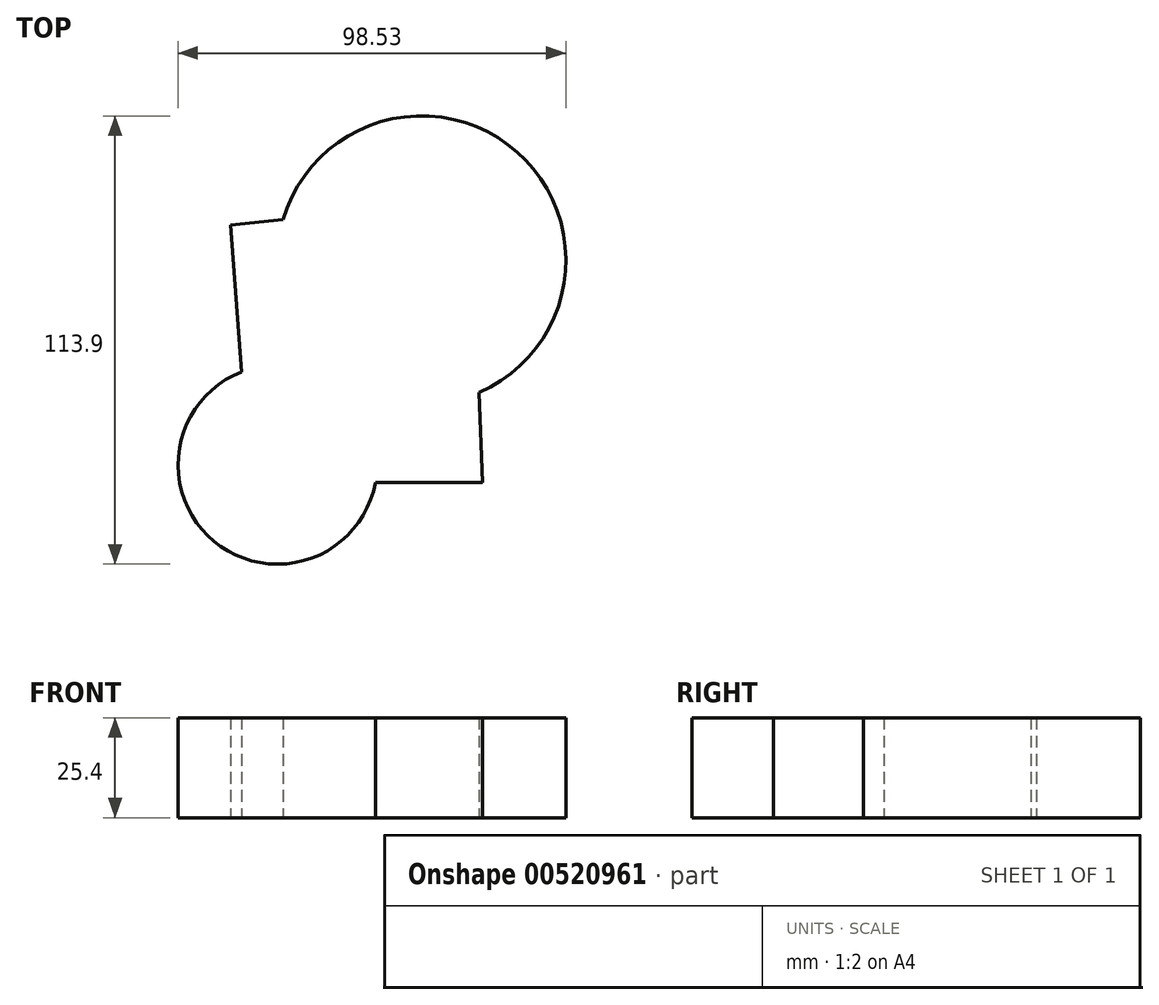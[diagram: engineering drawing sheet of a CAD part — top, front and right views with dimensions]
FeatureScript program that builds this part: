
annotation { "Feature Type Name" : "Feature", "Feature Type Description" : "" }
export const myFeature = defineFeature(function(context is Context, id is Id, definition is map)
    precondition{}
    {
        {
            var Q0;
            Q0=qCreatedBy(makeId("Top.planeOp"),FACE);
            var sketch = newSketch(context, id + "F0", { "sketchPlane" : qUnion([Q0])});
            skLineSegment(sketch, "E0", {"start": v(-48.47, 42.93) * mm, "end": v(-43.8, -19.86) * mm});
            skLineSegment(sketch, "E1", {"start": v(-43.8, -22.48) * mm, "end": v(15.48, -22.48) * mm});
            skLineSegment(sketch, "E2", {"start": v(15.48, -22.48) * mm, "end": v(12.85, 49.35) * mm});
            skLineSegment(sketch, "E3", {"start": v(12.85, 49.35) * mm, "end": v(-48.47, 42.93) * mm});
            skLineSegment(sketch, "E4", {"start": v(-43.8, -22.48) * mm, "end": v(-44.29, -13.34) * mm});
            skCircle(sketch, "E5", {"center": v(0, 34.04) * mm, "radius": 36.66 * mm});
            skCircle(sketch, "E6", {"center": v(-36.6, -17.94) * mm, "radius": 25.26 * mm});
            skSolve(sketch);
        }
        {
            var Q0;
            {var subQ0=sQuery(id+"F0.wireOp",EDGE,"E3");var subQ1=sQuery(id+"F0.wireOp",EDGE,"E2");var subQ2=makeQuery(id+"F0.imprint","INTERSECT",VERTEX,{"derivedFrom":[subQ1,subQ0]});Q0=makeQuery(id+"F0.imprint","IMPRINT",FACE,{"disambiguationData":[TD([[makeQuery(id+"F0.imprint","IMPRINT",EDGE,{"disambiguationData":[TD([[subQ2,1.0]])],"derivedFrom":subQ1}),1.0]])]});}
            var Q1;
            {var subQ0=sQuery(id+"F0.wireOp",EDGE,"E3");var subQ1=sQuery(id+"F0.wireOp",EDGE,"E2");var subQ2=makeQuery(id+"F0.imprint","INTERSECT",VERTEX,{"derivedFrom":[subQ1,subQ0]});Q1=makeQuery(id+"F0.imprint","IMPRINT",FACE,{"disambiguationData":[TD([[makeQuery(id+"F0.imprint","IMPRINT",EDGE,{"disambiguationData":[TD([[subQ2,1.0]])],"derivedFrom":subQ1}),-1.0]])]});}
            var Q2;
            {var subQ0=sQuery(id+"F0.wireOp",EDGE,"E4");Q2=makeQuery(id+"F0.imprint","IMPRINT",FACE,{"disambiguationData":[TD([[makeQuery(id+"F0.imprint","IMPRINT",EDGE,{"derivedFrom":subQ0}),1.0]])]});}
            var Q3;
            {var subQ0=sQuery(id+"F0.wireOp",EDGE,"E4");Q3=makeQuery(id+"F0.imprint","IMPRINT",FACE,{"disambiguationData":[TD([[makeQuery(id+"F0.imprint","IMPRINT",EDGE,{"derivedFrom":subQ0}),-1.0]])]});}
            var Q4;
            {var subQ0=sQuery(id+"F0.wireOp",EDGE,"E3");var subQ1=sQuery(id+"F0.wireOp",EDGE,"E0");var subQ2=makeQuery(id+"F0.imprint","INTERSECT",VERTEX,{"derivedFrom":[subQ1,subQ0]});Q4=makeQuery(id+"F0.imprint","IMPRINT",FACE,{"disambiguationData":[TD([[makeQuery(id+"F0.imprint","IMPRINT",EDGE,{"disambiguationData":[TD([[subQ2,-1.0]])],"derivedFrom":subQ1}),1.0]])]});}
            extrude(context, id + "F1", {"entities" : qUnion([Q0, Q1, Q2, Q3, Q4]), "depth" : 25.4 * mm, "offsetDistance" : 25.4 * mm});
        }
    });
